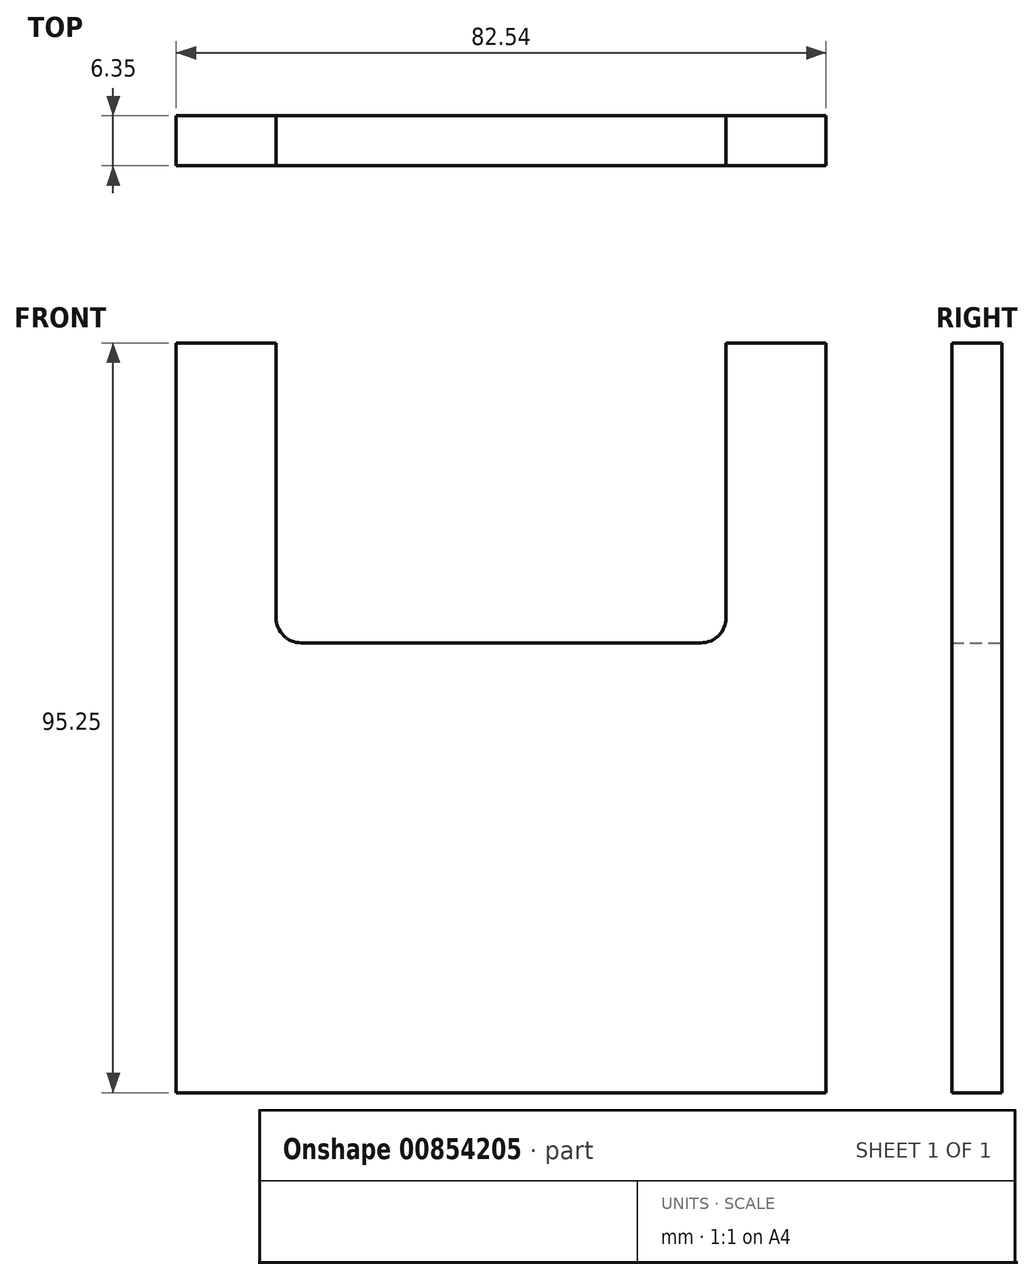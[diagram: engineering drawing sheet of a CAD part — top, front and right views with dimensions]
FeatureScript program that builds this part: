
annotation { "Feature Type Name" : "Feature", "Feature Type Description" : "" }
export const myFeature = defineFeature(function(context is Context, id is Id, definition is map)
    precondition{}
    {
        {
            var Q0;
            Q0=qCreatedBy(makeId("Front.planeOp"),FACE);
            var sketch = newSketch(context, id + "F0", { "sketchPlane" : qUnion([Q0])});
            skLineSegment(sketch, "E0", {"start": v(-41.27, 0) * mm, "end": v(-41.27, 95.25) * mm});
            skLineSegment(sketch, "E1", {"start": v(-41.27, 0) * mm, "end": v(41.27, 0) * mm});
            skLineSegment(sketch, "E2", {"start": v(41.28, 0) * mm, "end": v(41.28, 95.25) * mm});
            skLineSegment(sketch, "E3", {"start": v(41.27, 95.25) * mm, "end": v(28.58, 95.25) * mm});
            skLineSegment(sketch, "E4", {"start": v(28.57, 95.25) * mm, "end": v(28.58, 57.15) * mm});
            skLineSegment(sketch, "E5", {"start": v(-41.27, 95.25) * mm, "end": v(-28.58, 95.25) * mm});
            skLineSegment(sketch, "E6", {"start": v(-28.58, 95.25) * mm, "end": v(-28.57, 57.15) * mm});
            skLineSegment(sketch, "E7", {"start": v(28.58, 57.15) * mm, "end": v(-28.58, 57.15) * mm});
            skPoint(sketch, "E8.visualSharp", {"position": v(28.58, 57.15) * mm});
            skSolve(sketch);
        }
        {
            var Q0;
            Q0=makeQuery(id+"F0.imprint","IMPRINT",FACE,{"disambiguationData":[TD([[makeQuery(id+"F0.imprint","IMPRINT",EDGE,{"derivedFrom":sQuery(id+"F0.wireOp",EDGE,"E0")}),-1.0]])]});
            extrude(context, id + "F1", {"entities" : qUnion([Q0]), "depth" : 6.35 * mm, "offsetDistance" : 25.4 * mm});
        }
        {
            var Q0;
            Q0=makeQuery(id+"F1.opExtrude","SWEPT_EDGE",EDGE,{"disambiguationData":[OSD([sQuery(id+"F0.wireOp",EDGE,"E6"),sQuery(id+"F0.wireOp",EDGE,"E7")])]});
            var Q1;
            Q1=makeQuery(id+"F1.opExtrude","SWEPT_EDGE",EDGE,{"disambiguationData":[OSD([sQuery(id+"F0.wireOp",EDGE,"E4"),sQuery(id+"F0.wireOp",EDGE,"E7")])]});
            fillet(context, id + "F2", {"entities" : qUnion([Q0, Q1]), "radius" : 3.17 * mm, "tangentPropagation" : true, "allowEdgeOverflow" : false});
        }
    });
